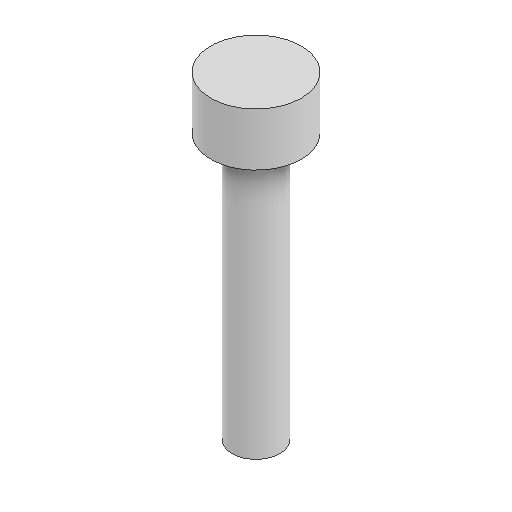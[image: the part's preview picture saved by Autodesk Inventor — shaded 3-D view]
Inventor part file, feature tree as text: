
AUTODESK INVENTOR PART (.ipt)
format: ipt  version: 2025 (Build 290162010, 162A)  size: 87,040 bytes
history: native  units: in
note: dims shown in document units (in); Inventor stores cm internally (conversion verified against a paired STEP export)
features: revolve x1, sketch x1
ambient origin geometry x8: Origin, YZ Plane, XZ Plane, XY Plane, X Axis, Y Axis, Z Axis, Center Point
bodies: Solid1 (feature_tree)
feature tree (2):
  revolve  "Revolution1"  [1 undecoded]
  sketch  "Sketch1"  dims[d1=0.265in d2=0.14in d3=0.155in d4=0.778in d5=90.0deg]
note: 1 required parameter value undecoded (feature->parameter linkage not recoverable at this tier; creation-order binding heuristic only, values carry confidence <= 0.55)
